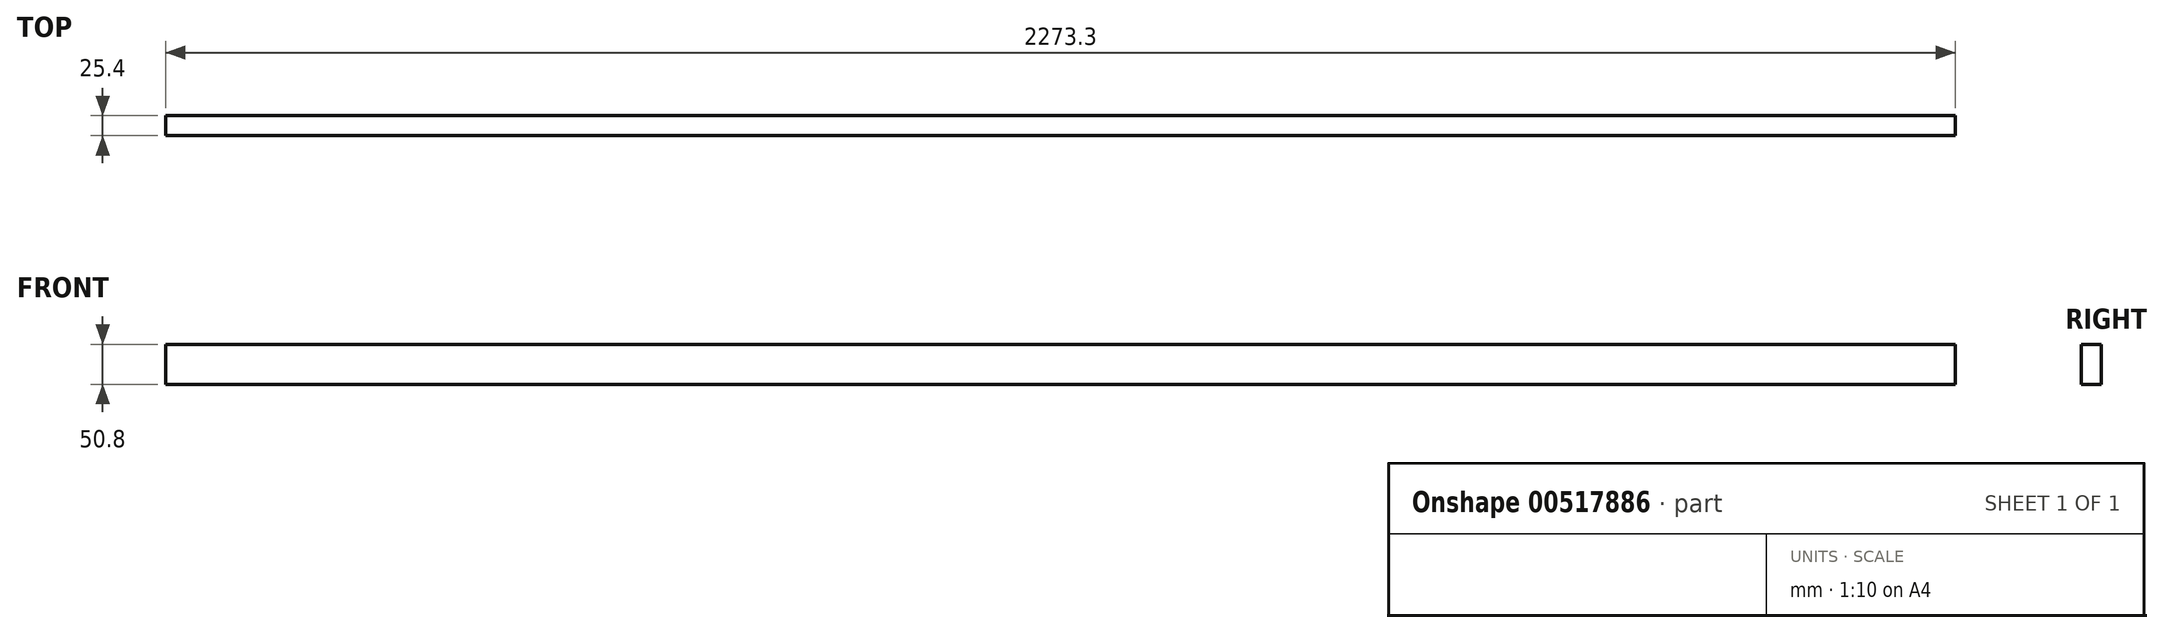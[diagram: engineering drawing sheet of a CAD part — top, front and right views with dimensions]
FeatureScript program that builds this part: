
annotation { "Feature Type Name" : "Feature", "Feature Type Description" : "" }
export const myFeature = defineFeature(function(context is Context, id is Id, definition is map)
    precondition{}
    {
        {
            var Q0;
            Q0=qCreatedBy(makeId("Right.planeOp"),FACE);
            var sketch = newSketch(context, id + "F0", { "sketchPlane" : qUnion([Q0])});
            skLineSegment(sketch, "E0.bottom", {"start": v(0, 0) * mm, "end": v(25.4, 0) * mm});
            skLineSegment(sketch, "E0.top", {"start": v(0, 50.8) * mm, "end": v(25.4, 50.8) * mm});
            skLineSegment(sketch, "E0.left", {"start": v(0, 0) * mm, "end": v(0, 50.8) * mm});
            skLineSegment(sketch, "E0.right", {"start": v(25.4, 0) * mm, "end": v(25.4, 50.8) * mm});
            skLineSegment(sketch, "E1.0", {"start": v(3.17, 47.63) * mm, "end": v(22.23, 47.63) * mm, "construction": true});
            skLineSegment(sketch, "E1.1", {"start": v(3.18, 3.18) * mm, "end": v(3.17, 47.63) * mm, "construction": true});
            skLineSegment(sketch, "E1.2", {"start": v(3.18, 3.18) * mm, "end": v(22.22, 3.18) * mm, "construction": true});
            skLineSegment(sketch, "E1.3", {"start": v(22.22, 3.18) * mm, "end": v(22.22, 47.63) * mm, "construction": true});
            skSolve(sketch);
        }
        {
            var Q0;
            Q0 = qSketchRegion(id + "F0", true);
            extrude(context, id + "F1", {"entities" : qUnion([Q0]), "oppositeDirection" : true, "depth" : 2273.3 * mm, "offsetDistance" : 25.4 * mm});
        }
    });
